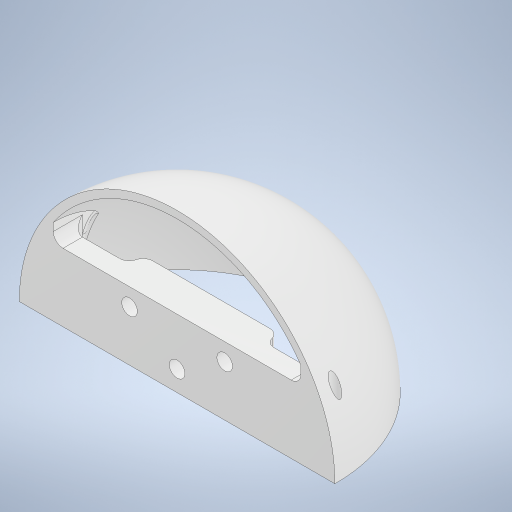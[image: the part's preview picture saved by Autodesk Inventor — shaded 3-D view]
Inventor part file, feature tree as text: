
AUTODESK INVENTOR PART (.ipt)
format: ipt  version: 2023 (Build 270158000, 158)  size: 420,352 bytes
history: native  units: mm
features: extrude x7, sketch x2, fillet x2, revolve x1, shell x1
ambient origin geometry x8: Origin, YZ Plane, XZ Plane, XY Plane, X Axis, Y Axis, Z Axis, Center Point
bodies: Volumenkörper1 (feature_tree)
feature tree (13):
  sketch  "Skizze1"  dims[d0=65.0mm d1=90.0deg d2=65.0mm]
  revolve  "Umdrehung1"
  extrude  "Extrusion4"  TaperAngle=90.0deg  [1 undecoded]
  shell  "Wandung2"  Thickness=65.0mm
  sketch  "Skizze2"  dims[d3=7.0mm d4=7.0mm d5=7.0mm d6=7.0mm d20=7.0mm d21=7.0mm d22=32.5mm d23=2.0mm d24=2.0mm d25=2.0mm d29=65.0mm d30=0.0mm d31=1.5mm d32=2.0mm d33=2.0mm d34=2.0mm d35=3.2mm d36=3.2mm d37=3.2mm d40=4.0mm d41=0.0mm d42=7.0mm d43=0.0mm d44=5.0mm d45=0.0mm d46=0.0mm d47=0.0mm d55=10.0mm d56=0.0mm d57=14.0mm d58=35.0mm d59=0.0mm d60=3.0mm d61=3.6mm d62=3.6mm d63=3.6mm d64=2.0mm d48=0.5mm d49=0.872665mm d65=0.0mm d66=0.0mm d67=0.0mm]
  extrude  "Extrusion6"  Depth=7.0mm
  extrude  "Extrusion7"  Depth=7.0mm
  extrude  "Extrusion8"  Depth=7.0mm
  extrude  "Extrusion9"  Depth=7.0mm
  extrude  "Extrusion10"  Depth=7.0mm
  extrude  "Extrusion11"  Depth=32.5mm
  fillet  "Rundung2"  Radius=2.0mm
  fillet  "Rundung3"  Radius=2.0mm
note: 1 required parameter value undecoded (feature->parameter linkage not recoverable at this tier; creation-order binding heuristic only, values carry confidence <= 0.55)
